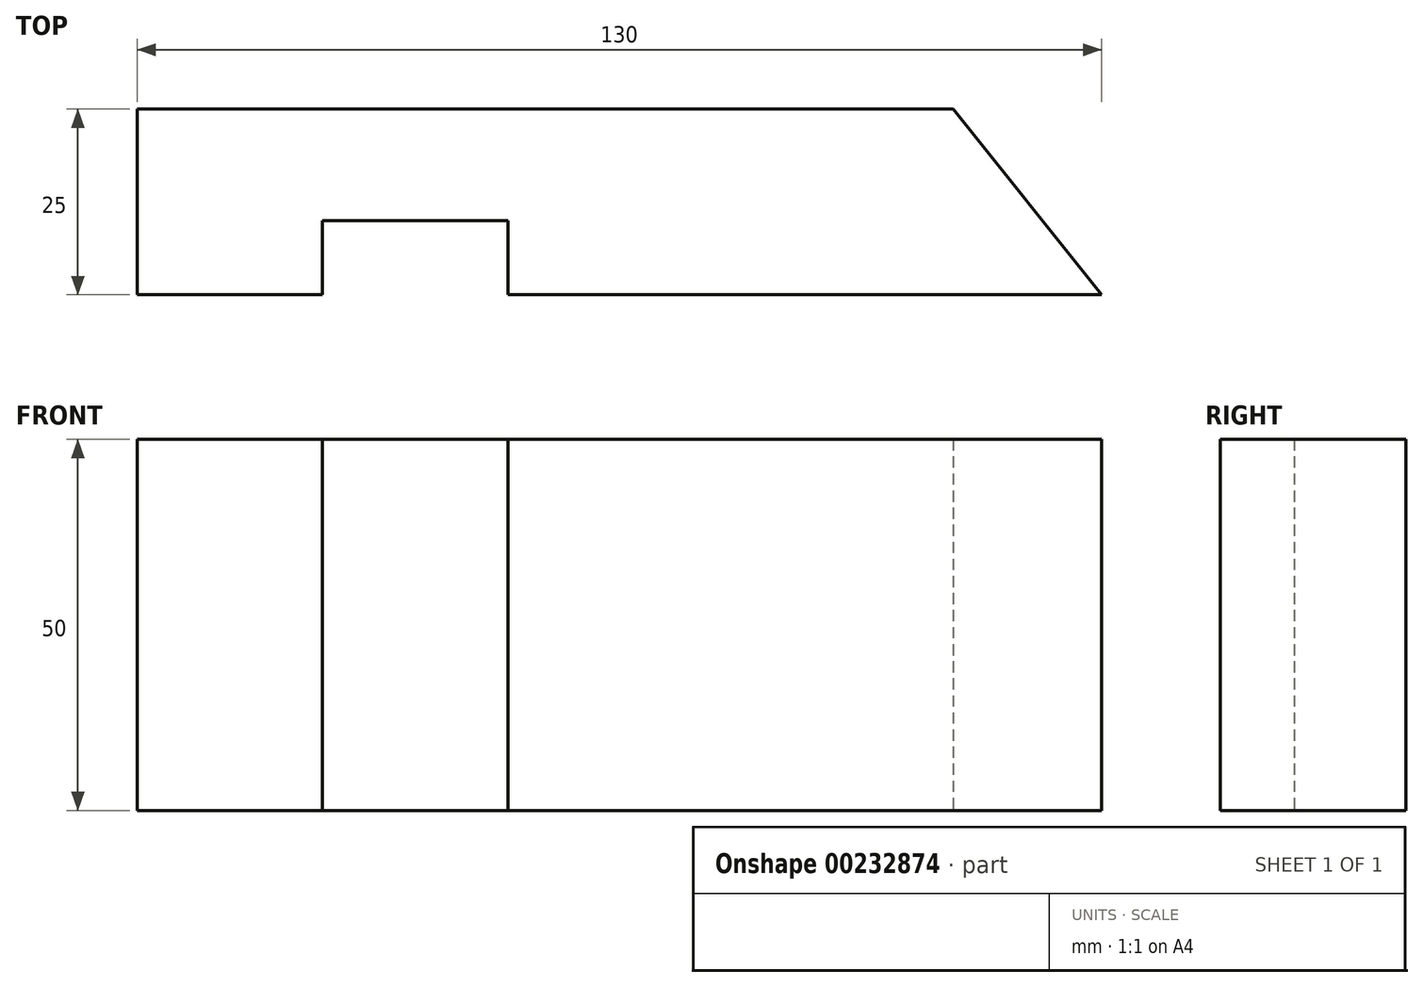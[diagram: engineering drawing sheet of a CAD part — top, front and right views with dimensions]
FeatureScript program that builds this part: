
annotation { "Feature Type Name" : "Feature", "Feature Type Description" : "" }
export const myFeature = defineFeature(function(context is Context, id is Id, definition is map)
    precondition{}
    {
        {
            var Q0;
            Q0=qCreatedBy(makeId("Top.planeOp"),FACE);
            var sketch = newSketch(context, id + "F0", { "sketchPlane" : qUnion([Q0])});
            skLineSegment(sketch, "E0", {"start": v(-65.12, 43.17) * mm, "end": v(44.88, 43.17) * mm});
            skLineSegment(sketch, "E1", {"start": v(44.88, 43.17) * mm, "end": v(64.88, 18.17) * mm});
            skLineSegment(sketch, "E2", {"start": v(64.88, 18.17) * mm, "end": v(-15.12, 18.17) * mm});
            skLineSegment(sketch, "E3", {"start": v(-15.12, 18.17) * mm, "end": v(-15.12, 28.17) * mm});
            skLineSegment(sketch, "E4", {"start": v(-15.12, 28.17) * mm, "end": v(-40.12, 28.17) * mm});
            skLineSegment(sketch, "E5", {"start": v(-40.12, 28.17) * mm, "end": v(-40.12, 18.17) * mm});
            skLineSegment(sketch, "E6", {"start": v(-40.12, 18.17) * mm, "end": v(-65.12, 18.17) * mm});
            skLineSegment(sketch, "E7", {"start": v(-65.12, 18.17) * mm, "end": v(-65.12, 43.17) * mm});
            skSolve(sketch);
        }
        {
            var Q0;
            Q0 = qSketchRegion(id + "F0", true);
            extrude(context, id + "F1", {"entities" : qUnion([Q0]), "depth" : 50 * mm});
        }
    });
